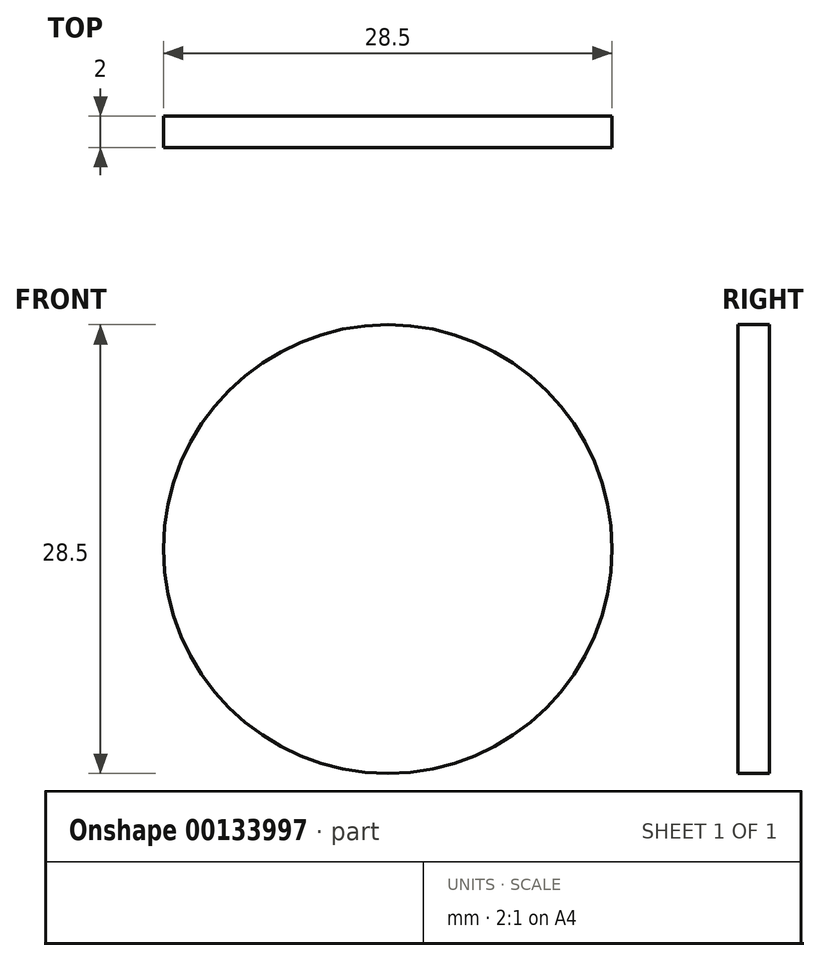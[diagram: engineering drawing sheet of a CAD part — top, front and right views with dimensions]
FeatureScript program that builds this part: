
annotation { "Feature Type Name" : "Feature", "Feature Type Description" : "" }
export const myFeature = defineFeature(function(context is Context, id is Id, definition is map)
    precondition{}
    {
        {
            var Q0;
            Q0=qCreatedBy(makeId("Front.planeOp"),FACE);
            var sketch = newSketch(context, id + "F0", { "sketchPlane" : qUnion([Q0])});
            skCircle(sketch, "E0", {"center": v(0, 0) * mm, "radius": 14.25 * mm});
            skSolve(sketch);
        }
        {
            var Q0;
            Q0 = qSketchRegion(id + "F0", true);
            extrude(context, id + "F1", {"entities" : qUnion([Q0]), "depth" : 2 * mm});
        }
    });
